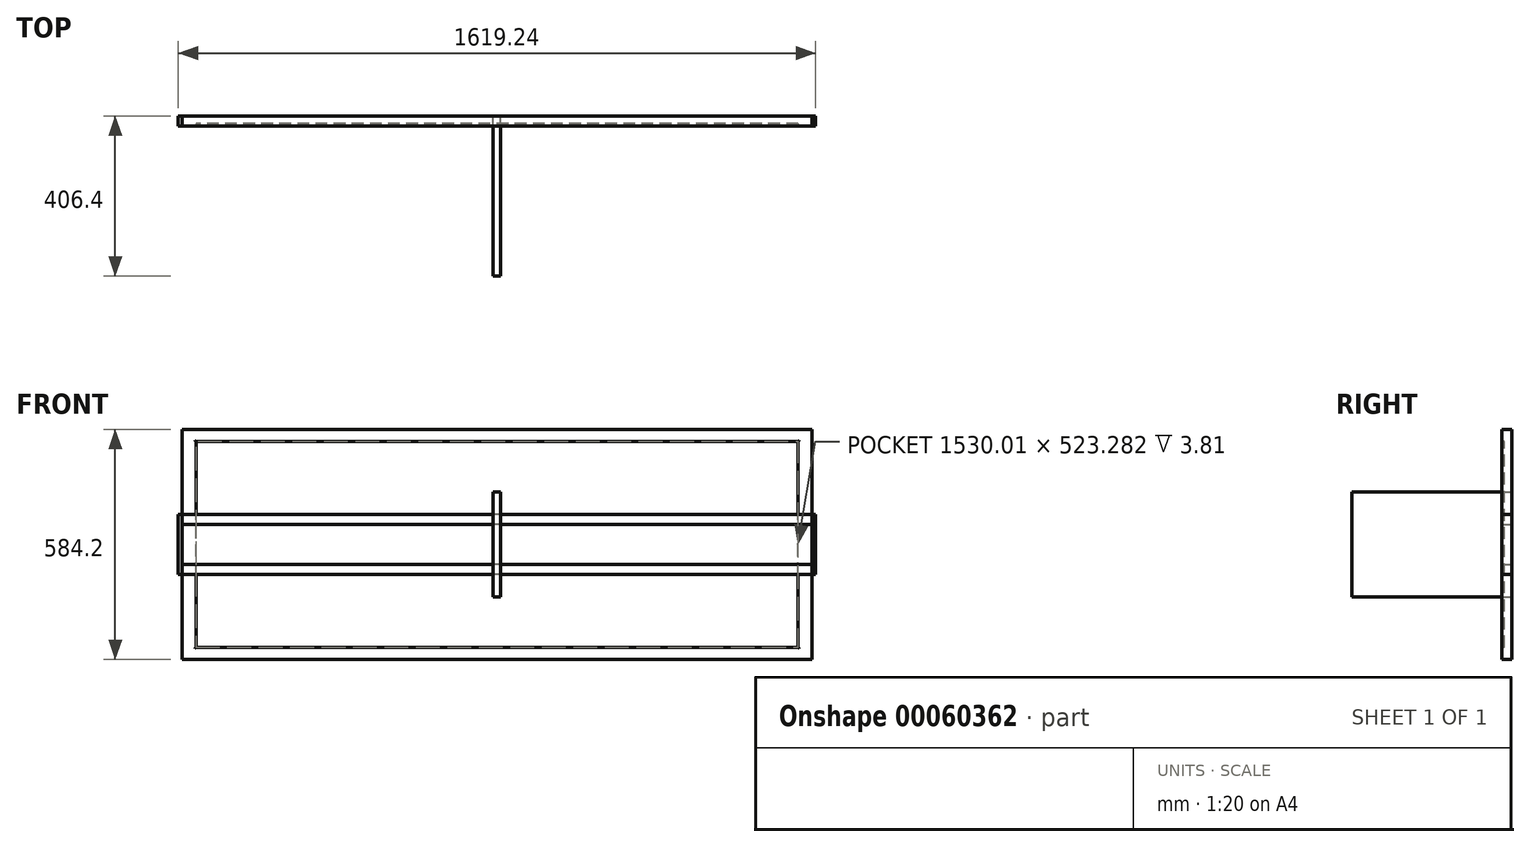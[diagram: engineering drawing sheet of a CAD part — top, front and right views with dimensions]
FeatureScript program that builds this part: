
annotation { "Feature Type Name" : "Feature", "Feature Type Description" : "" }
export const myFeature = defineFeature(function(context is Context, id is Id, definition is map)
    precondition{}
    {
        {
            var Q0;
            Q0=qCreatedBy(makeId("Front.planeOp"),FACE);
            var sketch = newSketch(context, id + "F0", { "sketchPlane" : qUnion([Q0])});
            skLineSegment(sketch, "E0.rect.bottom", {"start": v(9.52, -133.35) * mm, "end": v(-9.53, -133.35) * mm});
            skLineSegment(sketch, "E0.rect.top", {"start": v(9.53, 133.35) * mm, "end": v(-9.52, 133.35) * mm});
            skLineSegment(sketch, "E0.rect.left", {"start": v(9.52, -133.35) * mm, "end": v(9.53, 133.35) * mm});
            skLineSegment(sketch, "E0.rect.right", {"start": v(-9.53, -133.35) * mm, "end": v(-9.52, 133.35) * mm});
            skPoint(sketch, "E0.rect.middle", {"position": v(0, 0) * mm});
            skSolve(sketch);
        }
        {
            var Q0;
            Q0=makeQuery(id+"F0.imprint","IMPRINT",FACE,{"disambiguationData":[TD([[makeQuery(id+"F0.imprint","IMPRINT",EDGE,{"derivedFrom":sQuery(id+"F0.wireOp",EDGE,"E0.rect.bottom")}),-1.0]])]});
            extrude(context, id + "F1", {"entities" : qUnion([Q0]), "depth" : 406.4 * mm});
        }
        {
            var Q0;
            Q0=qCreatedBy(makeId("Front.planeOp"),FACE);
            var sketch = newSketch(context, id + "F2", { "sketchPlane" : qUnion([Q0])});
            skLineSegment(sketch, "E1.rect.bottom", {"start": v(800.1, 50.8) * mm, "end": v(-800.1, 50.8) * mm});
            skLineSegment(sketch, "E1.rect.top", {"start": v(800.1, -50.8) * mm, "end": v(-800.1, -50.8) * mm});
            skLineSegment(sketch, "E1.rect.left", {"start": v(800.1, 50.8) * mm, "end": v(800.1, -50.8) * mm});
            skLineSegment(sketch, "E1.rect.right", {"start": v(-800.1, 50.8) * mm, "end": v(-800.1, -50.8) * mm});
            skPoint(sketch, "E1.rect.middle", {"position": v(0, 0) * mm});
            skSolve(sketch);
        }
        {
            var Q0;
            Q0=qCreatedBy(makeId("Front.planeOp"),FACE);
            var sketch = newSketch(context, id + "F3", { "sketchPlane" : qUnion([Q0])});
            skLineSegment(sketch, "E2.rect.bottom", {"start": v(50.8, -422.28) * mm, "end": v(-50.8, -422.28) * mm});
            skLineSegment(sketch, "E2.rect.top", {"start": v(50.8, 422.28) * mm, "end": v(-50.8, 422.28) * mm});
            skLineSegment(sketch, "E2.rect.left", {"start": v(50.8, -422.28) * mm, "end": v(50.8, 422.28) * mm});
            skLineSegment(sketch, "E2.rect.right", {"start": v(-50.8, -422.28) * mm, "end": v(-50.8, 422.28) * mm});
            skPoint(sketch, "E2.rect.middle", {"position": v(0, 0) * mm});
            skSolve(sketch);
        }
        {
            var Q0;
            Q0=makeQuery(id+"F2.imprint","IMPRINT",FACE,{"disambiguationData":[TD([[makeQuery(id+"F2.imprint","IMPRINT",EDGE,{"derivedFrom":sQuery(id+"F2.wireOp",EDGE,"E1.rect.bottom")}),1.0]])]});
            extrude(context, id + "F4", {"entities" : qUnion([Q0]), "depth" : 25.4 * mm});
        }
        {
            var Q0;
            Q0=qCreatedBy(makeId("Front.planeOp"),FACE);
            var sketch = newSketch(context, id + "F5", { "sketchPlane" : qUnion([Q0])});
            skLineSegment(sketch, "E3.rect.bottom", {"start": v(800.1, -292.1) * mm, "end": v(-800.1, -292.1) * mm});
            skLineSegment(sketch, "E3.rect.top", {"start": v(800.1, 292.1) * mm, "end": v(-800.1, 292.1) * mm});
            skLineSegment(sketch, "E3.rect.left", {"start": v(800.1, -292.1) * mm, "end": v(800.1, 292.1) * mm});
            skLineSegment(sketch, "E3.rect.right", {"start": v(-800.1, -292.1) * mm, "end": v(-800.1, 292.1) * mm});
            skPoint(sketch, "E3.rect.middle", {"position": v(0, 0) * mm});
            skSolve(sketch);
        }
        {
            var Q0;
            Q0=makeQuery(id+"F5.imprint","IMPRINT",FACE,{"disambiguationData":[TD([[makeQuery(id+"F5.imprint","IMPRINT",EDGE,{"derivedFrom":sQuery(id+"F5.wireOp",EDGE,"E3.rect.bottom")}),-1.0]])]});
            extrude(context, id + "F6", {"entities" : qUnion([Q0]), "depth" : 25.4 * mm});
        }
        {
            var Q0;
            Q0=qCreatedBy(makeId("Front.planeOp"),FACE);
            var sketch = newSketch(context, id + "F7", { "sketchPlane" : qUnion([Q0])});
            skLineSegment(sketch, "E4.rect.bottom", {"start": v(809.62, -76.2) * mm, "end": v(-809.62, -76.2) * mm});
            skLineSegment(sketch, "E4.rect.top", {"start": v(809.62, 76.2) * mm, "end": v(-809.62, 76.2) * mm});
            skLineSegment(sketch, "E4.rect.left", {"start": v(809.62, -76.2) * mm, "end": v(809.62, 76.2) * mm});
            skLineSegment(sketch, "E4.rect.right", {"start": v(-809.62, -76.2) * mm, "end": v(-809.62, 76.2) * mm});
            skPoint(sketch, "E4.rect.middle", {"position": v(0, 0) * mm});
            skSolve(sketch);
        }
        {
            var Q0;
            Q0 = qSketchRegion(id + "F7", true);
            extrude(context, id + "F8", {"entities" : qUnion([Q0]), "depth" : 25.4 * mm});
        }
        {
            var Q0;
            Q0=makeQuery(id+"F6.opExtrude","CAP_FACE",FACE,{"disambiguationData":[OSD([sQuery(id+"F5.wireOp",EDGE,"E3.rect.bottom"),sQuery(id+"F5.wireOp",EDGE,"E3.rect.top"),sQuery(id+"F5.wireOp",EDGE,"E3.rect.left"),sQuery(id+"F5.wireOp",EDGE,"E3.rect.right")])],"isStart":false});
            var sketch = newSketch(context, id + "F9", { "sketchPlane" : qUnion([Q0])});
            skLineSegment(sketch, "E5.rect.bottom", {"start": v(765, -261.64) * mm, "end": v(-765, -261.64) * mm});
            skLineSegment(sketch, "E5.rect.top", {"start": v(765, 261.64) * mm, "end": v(-765, 261.64) * mm});
            skLineSegment(sketch, "E5.rect.left", {"start": v(765, -261.64) * mm, "end": v(765, 261.64) * mm});
            skLineSegment(sketch, "E5.rect.right", {"start": v(-765, -261.64) * mm, "end": v(-765, 261.64) * mm});
            skPoint(sketch, "E5.rect.middle", {"position": v(0, 0) * mm});
            skSolve(sketch);
        }
        {
            var Q0;
            Q0=makeQuery(id+"F9.imprint","IMPRINT",FACE,{"disambiguationData":[TD([[makeQuery(id+"F9.imprint","IMPRINT",EDGE,{"derivedFrom":sQuery(id+"F9.wireOp",EDGE,"E5.rect.bottom")}),-1.0]])]});
            extrude(context, id + "F10", {"entities" : qUnion([Q0]), "endBound" : BoundingType.SYMMETRIC, "oppositeDirection" : true, "depth" : 12.7 * mm});
        }
        {
            var Q0;
            Q0=makeQuery(id+"F10.opExtrude","SWEPT_BODY",BODY,{"disambiguationData":[OSD([sQuery(id+"F9.wireOp",EDGE,"E5.rect.bottom"),sQuery(id+"F9.wireOp",EDGE,"E5.rect.top"),sQuery(id+"F9.wireOp",EDGE,"E5.rect.left"),sQuery(id+"F9.wireOp",EDGE,"E5.rect.right")])]});
            var Q1;
            Q1=makeQuery(id+"F6.opExtrude","SWEPT_BODY",BODY,{"disambiguationData":[OSD([sQuery(id+"F5.wireOp",EDGE,"E3.rect.bottom"),sQuery(id+"F5.wireOp",EDGE,"E3.rect.top"),sQuery(id+"F5.wireOp",EDGE,"E3.rect.left"),sQuery(id+"F5.wireOp",EDGE,"E3.rect.right")])]});
            booleanBodies(context, id + "F11", {"operationType" : BooleanOperationType.SUBTRACTION, "tools" : qUnion([Q0]), "targets" : qUnion([Q1])});
        }
        {
            var Q0;
            Q0=makeQuery(id+"F11.opBoolean","INTERSECT",EDGE,{"derivedFrom":[makeQuery(id+"F6.opExtrude","CAP_FACE",FACE,{"disambiguationData":[OSD([sQuery(id+"F5.wireOp",EDGE,"E3.rect.bottom"),sQuery(id+"F5.wireOp",EDGE,"E3.rect.top"),sQuery(id+"F5.wireOp",EDGE,"E3.rect.left"),sQuery(id+"F5.wireOp",EDGE,"E3.rect.right")])],"isStart":false}),makeQuery(id+"F10.opExtrude","SWEPT_FACE",FACE,{"disambiguationData":[OSD([sQuery(id+"F9.wireOp",EDGE,"E5.rect.top")])]})]});
            var Q1;
            Q1=makeQuery(id+"F11.opBoolean","INTERSECT",EDGE,{"derivedFrom":[makeQuery(id+"F6.opExtrude","CAP_FACE",FACE,{"disambiguationData":[OSD([sQuery(id+"F5.wireOp",EDGE,"E3.rect.bottom"),sQuery(id+"F5.wireOp",EDGE,"E3.rect.top"),sQuery(id+"F5.wireOp",EDGE,"E3.rect.left"),sQuery(id+"F5.wireOp",EDGE,"E3.rect.right")])],"isStart":false}),makeQuery(id+"F10.opExtrude","SWEPT_FACE",FACE,{"disambiguationData":[OSD([sQuery(id+"F9.wireOp",EDGE,"E5.rect.right")])]})]});
            var Q2;
            Q2=makeQuery(id+"F11.opBoolean","INTERSECT",EDGE,{"derivedFrom":[makeQuery(id+"F6.opExtrude","CAP_FACE",FACE,{"disambiguationData":[OSD([sQuery(id+"F5.wireOp",EDGE,"E3.rect.bottom"),sQuery(id+"F5.wireOp",EDGE,"E3.rect.top"),sQuery(id+"F5.wireOp",EDGE,"E3.rect.left"),sQuery(id+"F5.wireOp",EDGE,"E3.rect.right")])],"isStart":false}),makeQuery(id+"F10.opExtrude","SWEPT_FACE",FACE,{"disambiguationData":[OSD([sQuery(id+"F9.wireOp",EDGE,"E5.rect.bottom")])]})]});
            var Q3;
            Q3=makeQuery(id+"F11.opBoolean","INTERSECT",EDGE,{"derivedFrom":[makeQuery(id+"F6.opExtrude","CAP_FACE",FACE,{"disambiguationData":[OSD([sQuery(id+"F5.wireOp",EDGE,"E3.rect.bottom"),sQuery(id+"F5.wireOp",EDGE,"E3.rect.top"),sQuery(id+"F5.wireOp",EDGE,"E3.rect.left"),sQuery(id+"F5.wireOp",EDGE,"E3.rect.right")])],"isStart":false}),makeQuery(id+"F10.opExtrude","SWEPT_FACE",FACE,{"disambiguationData":[OSD([sQuery(id+"F9.wireOp",EDGE,"E5.rect.left")])]})]});
            fillet(context, id + "F12", {"entities" : qUnion([Q0, Q1, Q2, Q3]), "radius" : 2.54 * mm, "tangentPropagation" : true, "allowEdgeOverflow" : false});
        }
    });
